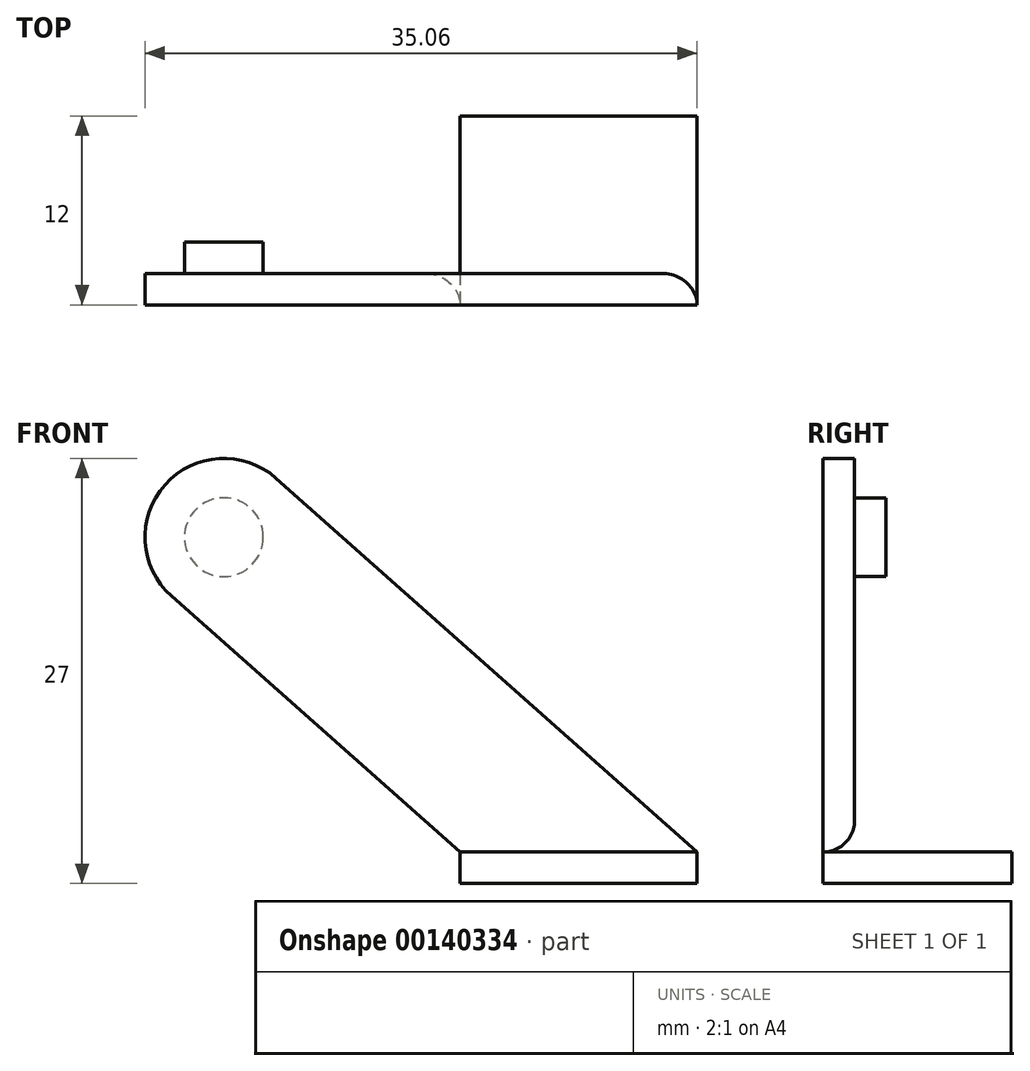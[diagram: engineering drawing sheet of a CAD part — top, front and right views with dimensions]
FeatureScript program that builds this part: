
annotation { "Feature Type Name" : "Feature", "Feature Type Description" : "" }
export const myFeature = defineFeature(function(context is Context, id is Id, definition is map)
    precondition{}
    {
        {
            var Q0;
            Q0=qCreatedBy(makeId("Front.planeOp"),FACE);
            var sketch = newSketch(context, id + "F0", { "sketchPlane" : qUnion([Q0])});
            skPoint(sketch, "E0.middle", {"position": v(0, 0) * mm});
            skCircle(sketch, "E1", {"center": v(0, 0) * mm, "radius": 2.5 * mm});
            skArc(sketch, "E2", {"start": v(3.32, 3.74) * mm, "mid": v(-3.74, 3.32) * mm, "end": v(-3.32, -3.74) * mm});
            skLineSegment(sketch, "E3", {"start": v(15, -20) * mm, "end": v(-3.32, -3.74) * mm});
            skLineSegment(sketch, "E4", {"start": v(3.32, 3.74) * mm, "end": v(30.06, -20) * mm});
            skLineSegment(sketch, "E5", {"start": v(15, -20) * mm, "end": v(30.06, -20) * mm});
            skPoint(sketch, "E0.top.start.orphan", {"position": v(5, 20) * mm});
            skPoint(sketch, "E6.orphan", {"position": v(-5, 20) * mm});
            skPoint(sketch, "E0.bottom.end.orphan", {"position": v(-5, -20) * mm});
            skPoint(sketch, "E7.start.orphan", {"position": v(5, -20) * mm});
            skLineSegment(sketch, "E8", {"start": v(15, -20) * mm, "end": v(15, -22) * mm});
            skLineSegment(sketch, "E9", {"start": v(15, -22) * mm, "end": v(30.06, -22) * mm});
            skLineSegment(sketch, "E10", {"start": v(30.06, -22) * mm, "end": v(30.06, -20) * mm});
            skSolve(sketch);
        }
        {
            var Q0;
            Q0=makeQuery(id+"F0.imprint","IMPRINT",FACE,{"disambiguationData":[TD([[makeQuery(id+"F0.imprint","IMPRINT",EDGE,{"derivedFrom":sQuery(id+"F0.wireOp",EDGE,"E1")}),-1.0]])]});
            extrude(context, id + "F1", {"entities" : qUnion([Q0]), "depth" : 2 * mm});
        }
        {
            var Q0;
            {var subQ1=sQuery(id+"F0.wireOp",EDGE,"E8");Q0=makeQuery(id+"F0.imprint","IMPRINT",FACE,{"disambiguationData":[TD([[makeQuery(id+"F0.imprint","IMPRINT",EDGE,{"derivedFrom":subQ1}),1.0]])]});}
            extrude(context, id + "F2", {"entities" : qUnion([Q0]), "oppositeDirection" : true, "depth" : 10 * mm, "hasSecondDirection" : true, "secondDirectionOppositeDirection" : false, "secondDirectionDepth" : 2 * mm});
        }
        {
            var Q0;
            Q0=makeQuery(id+"F0.imprint","IMPRINT",FACE,{"disambiguationData":[TD([[makeQuery(id+"F0.imprint","IMPRINT",EDGE,{"derivedFrom":sQuery(id+"F0.wireOp",EDGE,"E1")}),1.0]])]});
            extrude(context, id + "F3", {"entities" : qUnion([Q0]), "operationType" : NewBodyOperationType.ADD, "depth" : 2 * mm, "hasSecondDirection" : true, "secondDirectionOppositeDirection" : true, "secondDirectionDepth" : 2 * mm});
        }
        {
            var Q0;
            Q0=makeQuery(id+"F1.opExtrude","CAP_EDGE",EDGE,{"disambiguationData":[OSD([sQuery(id+"F0.wireOp",EDGE,"E5")])],"isStart":true});
            fillet(context, id + "F4", {"entities" : qUnion([Q0]), "radius" : 2 * mm, "tangentPropagation" : true, "allowEdgeOverflow" : false});
        }
    });
